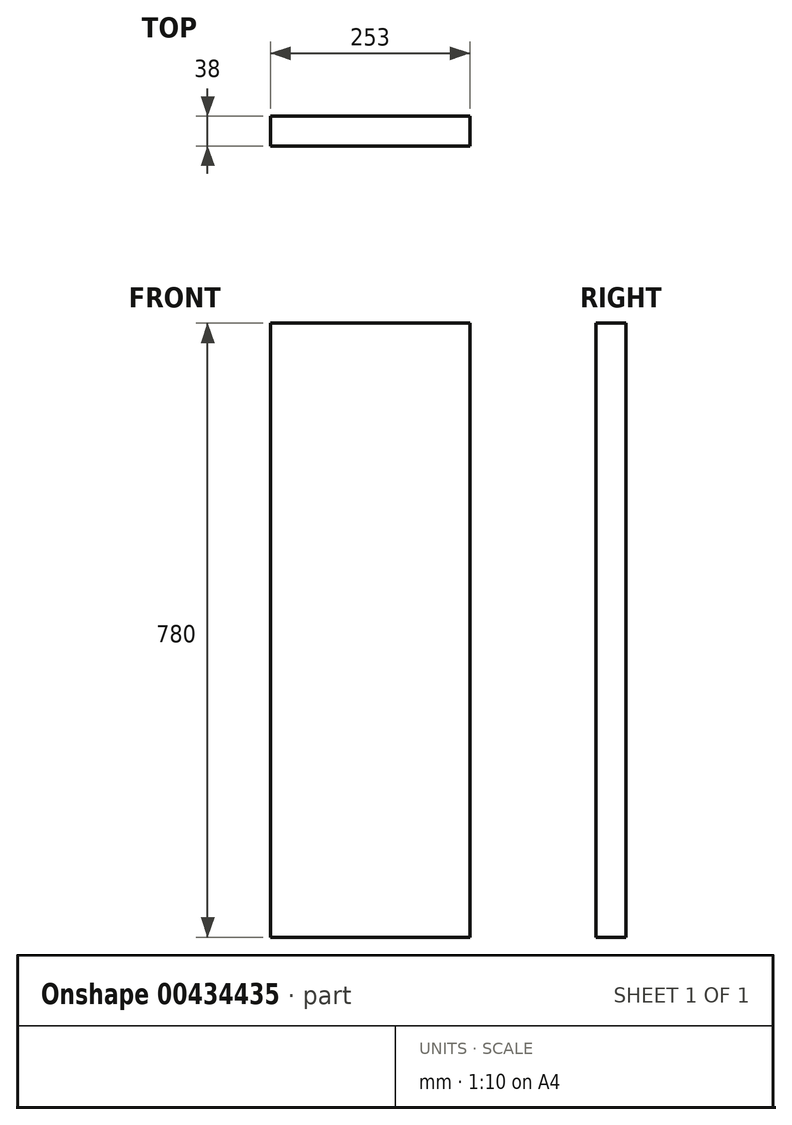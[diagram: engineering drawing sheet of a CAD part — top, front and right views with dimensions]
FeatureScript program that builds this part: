
annotation { "Feature Type Name" : "Feature", "Feature Type Description" : "" }
export const myFeature = defineFeature(function(context is Context, id is Id, definition is map)
    precondition{}
    {
        {
            var Q0;
            Q0=qCreatedBy(makeId("Front.planeOp"),FACE);
            var sketch = newSketch(context, id + "F0", { "sketchPlane" : qUnion([Q0])});
            skLineSegment(sketch, "E0.bottom", {"start": v(-126.5, 390) * mm, "end": v(126.5, 390) * mm});
            skLineSegment(sketch, "E0.top", {"start": v(-126.5, -390) * mm, "end": v(126.5, -390) * mm});
            skLineSegment(sketch, "E0.left", {"start": v(-126.5, 390) * mm, "end": v(-126.5, -390) * mm});
            skLineSegment(sketch, "E0.right", {"start": v(126.5, 390) * mm, "end": v(126.5, -390) * mm});
            skLineSegment(sketch, "E1", {"start": v(-126.5, 390) * mm, "end": v(126.5, -390) * mm, "construction": true});
            skSolve(sketch);
        }
        {
            var Q0;
            Q0 = qSketchRegion(id + "F0", true);
            extrude(context, id + "F1", {"entities" : qUnion([Q0]), "endBound" : BoundingType.SYMMETRIC, "depth" : 38 * mm, "offsetDistance" : 25 * mm});
        }
    });
